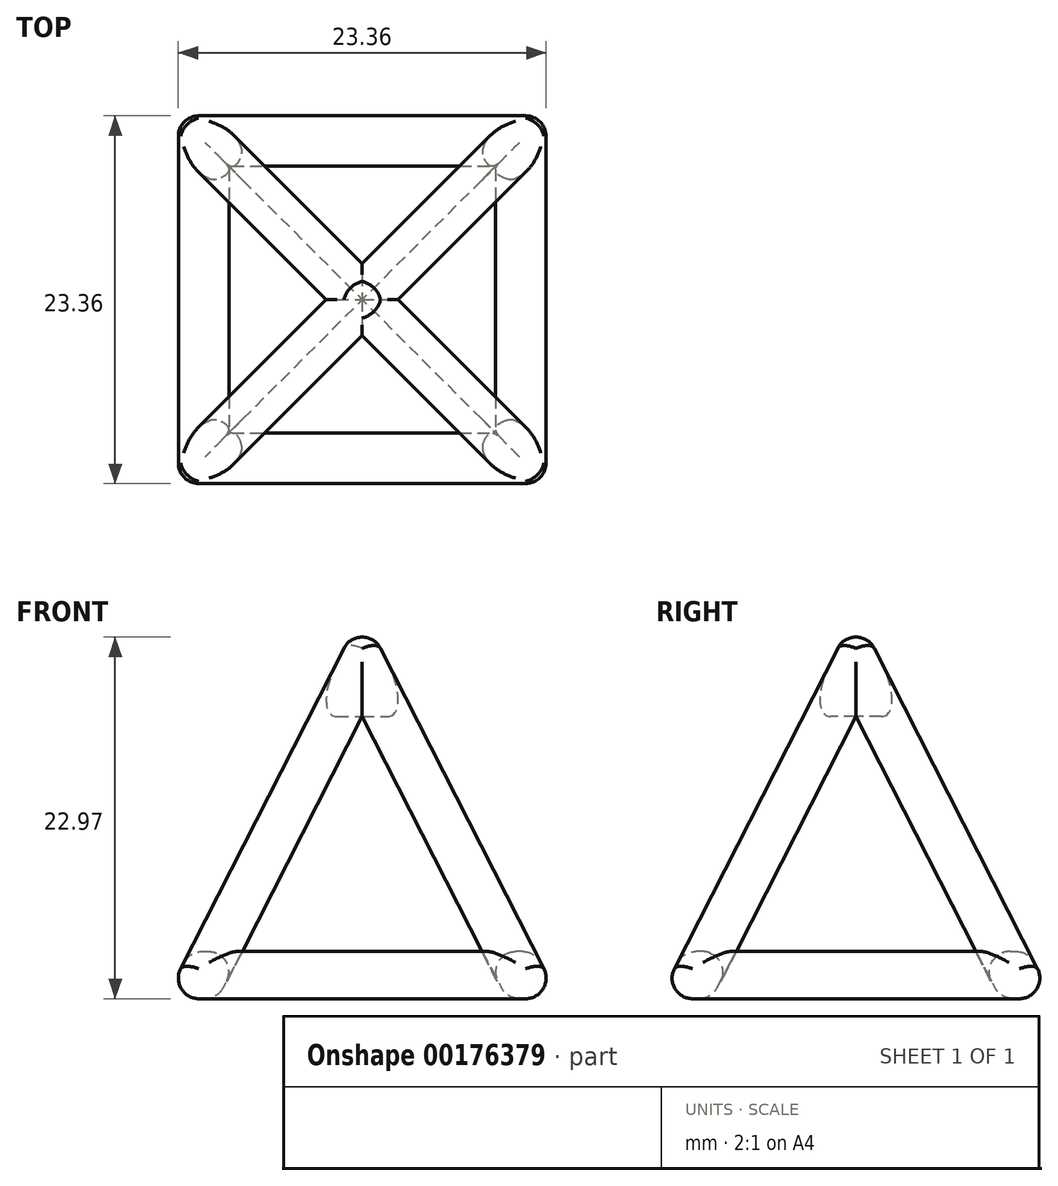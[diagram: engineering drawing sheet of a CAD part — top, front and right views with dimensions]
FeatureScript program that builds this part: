
annotation { "Feature Type Name" : "Feature", "Feature Type Description" : "" }
export const myFeature = defineFeature(function(context is Context, id is Id, definition is map)
    precondition{}
    {
        {
            var Q0;
            Q0=qCreatedBy(makeId("Top.planeOp"),FACE);
            cPlane(context, id + "F0", {"entities" : qUnion([Q0]), "cplaneType" : CPlaneType.OFFSET, "offset" : 25 * mm, "width" : 150 * mm, "height" : 150 * mm});
        }
        {
            var Q0;
            Q0=qCreatedBy(makeId("Top.planeOp"),FACE);
            var sketch = newSketch(context, id + "F1", { "sketchPlane" : qUnion([Q0])});
            skLineSegment(sketch, "E0.bottom", {"start": v(12.5, -12.5) * mm, "end": v(-12.5, -12.5) * mm});
            skLineSegment(sketch, "E0.top", {"start": v(12.5, 12.5) * mm, "end": v(-12.5, 12.5) * mm});
            skLineSegment(sketch, "E0.left", {"start": v(12.5, -12.5) * mm, "end": v(12.5, 12.5) * mm});
            skLineSegment(sketch, "E0.right", {"start": v(-12.5, -12.5) * mm, "end": v(-12.5, 12.5) * mm});
            skPoint(sketch, "E0.middle", {"position": v(0, 0) * mm});
            skSolve(sketch);
        }
        {
            var Q0;
            Q0 = qSketchRegion(id + "F1", true);
            extrude(context, id + "F2", {"entities" : qUnion([Q0]), "depth" : 30 * mm, "hasDraft" : true, "draftAngle" : 27 * degree, "draftPullDirection" : true});
        }
        {
            var Q0;
            Q0=makeQuery(id+"F2.opExtrude","CAP_FACE",FACE,{"disambiguationData":[OSD([sQuery(id+"F1.wireOp",EDGE,"E0.bottom"),sQuery(id+"F1.wireOp",EDGE,"E0.top"),sQuery(id+"F1.wireOp",EDGE,"E0.left"),sQuery(id+"F1.wireOp",EDGE,"E0.right")])],"isStart":true});
            var sketch = newSketch(context, id + "F3", { "sketchPlane" : qUnion([Q0])});
            skLineSegment(sketch, "E1.0", {"start": v(9.2, 9.2) * mm, "end": v(-9.2, 9.2) * mm});
            skLineSegment(sketch, "E1.1", {"start": v(9.2, 9.2) * mm, "end": v(9.2, -9.2) * mm});
            skLineSegment(sketch, "E1.2", {"start": v(9.2, -9.2) * mm, "end": v(-9.2, -9.2) * mm});
            skLineSegment(sketch, "E1.3", {"start": v(-9.2, 9.2) * mm, "end": v(-9.2, -9.2) * mm});
            skSolve(sketch);
        }
        {
            var Q0;
            Q0 = qSketchRegion(id + "F3", true);
            extrude(context, id + "F4", {"entities" : qUnion([Q0]), "operationType" : NewBodyOperationType.REMOVE, "oppositeDirection" : true, "depth" : 25 * mm, "hasDraft" : true, "draftAngle" : 28 * degree, "draftPullDirection" : true});
        }
        {
            var Q0;
            Q0=qCreatedBy(makeId("Front.planeOp"),FACE);
            var sketch = newSketch(context, id + "F5", { "sketchPlane" : qUnion([Q0])});
            skLineSegment(sketch, "E2.0", {"start": v(0, 17.92) * mm, "end": v(-7.6, 3) * mm});
            skLineSegment(sketch, "E2.1", {"start": v(0, 17.92) * mm, "end": v(7.6, 3) * mm});
            skLineSegment(sketch, "E2.2", {"start": v(7.6, 3) * mm, "end": v(-7.6, 3) * mm});
            skSolve(sketch);
        }
        {
            var Q0;
            Q0 = qSketchRegion(id + "F5", true);
            extrude(context, id + "F6", {"entities" : qUnion([Q0]), "operationType" : NewBodyOperationType.REMOVE, "oppositeDirection" : true, "depth" : 25 * mm, "hasSecondDirection" : true, "secondDirectionOppositeDirection" : false, "secondDirectionDepth" : 25 * mm});
        }
        {
            var Q0;
            Q0=qCreatedBy(makeId("Right.planeOp"),FACE);
            var sketch = newSketch(context, id + "F7", { "sketchPlane" : qUnion([Q0])});
            skLineSegment(sketch, "E3.0", {"start": v(0, 17.92) * mm, "end": v(7.6, 3) * mm});
            skLineSegment(sketch, "E3.1", {"start": v(0, 17.92) * mm, "end": v(-7.6, 3) * mm});
            skLineSegment(sketch, "E3.2", {"start": v(-7.6, 3) * mm, "end": v(7.6, 3) * mm});
            skSolve(sketch);
        }
        {
            var Q0;
            Q0 = qSketchRegion(id + "F7", true);
            extrude(context, id + "F8", {"entities" : qUnion([Q0]), "operationType" : NewBodyOperationType.REMOVE, "oppositeDirection" : true, "depth" : 25 * mm, "hasSecondDirection" : true, "secondDirectionOppositeDirection" : false, "secondDirectionDepth" : 25 * mm});
        }
        {
            var Q0;
            Q0=makeQuery(id+"F2.opExtrude","SWEPT_FACE",FACE,{"disambiguationData":[OSD([sQuery(id+"F1.wireOp",EDGE,"E0.bottom")])]});
            var Q1;
            Q1=makeQuery(id+"F2.opExtrude","SWEPT_FACE",FACE,{"disambiguationData":[OSD([sQuery(id+"F1.wireOp",EDGE,"E0.top")])]});
            var Q2;
            Q2=makeQuery(id+"F2.opExtrude","CAP_FACE",FACE,{"disambiguationData":[OSD([sQuery(id+"F1.wireOp",EDGE,"E0.bottom"),sQuery(id+"F1.wireOp",EDGE,"E0.top"),sQuery(id+"F1.wireOp",EDGE,"E0.left"),sQuery(id+"F1.wireOp",EDGE,"E0.right")])],"isStart":true});
            var Q3;
            Q3=makeQuery(id+"F8.boolean.opBoolean","INTERSECT",EDGE,{"derivedFrom":[makeQuery(id+"F2.opExtrude","SWEPT_FACE",FACE,{"disambiguationData":[OSD([sQuery(id+"F1.wireOp",EDGE,"E0.left")])]}),makeQuery(id+"F8.opExtrude","SWEPT_FACE",FACE,{"disambiguationData":[OSD([sQuery(id+"F7.wireOp",EDGE,"E3.2")])]})]});
            var Q4;
            Q4=makeQuery(id+"F8.boolean.opBoolean","INTERSECT",EDGE,{"derivedFrom":[makeQuery(id+"F2.opExtrude","SWEPT_FACE",FACE,{"disambiguationData":[OSD([sQuery(id+"F1.wireOp",EDGE,"E0.left")])]}),makeQuery(id+"F8.opExtrude","SWEPT_FACE",FACE,{"disambiguationData":[OSD([sQuery(id+"F7.wireOp",EDGE,"E3.0")])]})]});
            var Q5;
            Q5=makeQuery(id+"F8.boolean.opBoolean","INTERSECT",EDGE,{"derivedFrom":[makeQuery(id+"F2.opExtrude","SWEPT_FACE",FACE,{"disambiguationData":[OSD([sQuery(id+"F1.wireOp",EDGE,"E0.left")])]}),makeQuery(id+"F8.opExtrude","SWEPT_FACE",FACE,{"disambiguationData":[OSD([sQuery(id+"F7.wireOp",EDGE,"E3.1")])]})]});
            var Q6;
            Q6=makeQuery(id+"F8.boolean.opBoolean","INTERSECT",EDGE,{"derivedFrom":[makeQuery(id+"F2.opExtrude","SWEPT_FACE",FACE,{"disambiguationData":[OSD([sQuery(id+"F1.wireOp",EDGE,"E0.right")])]}),makeQuery(id+"F8.opExtrude","SWEPT_FACE",FACE,{"disambiguationData":[OSD([sQuery(id+"F7.wireOp",EDGE,"E3.1")])]})]});
            var Q7;
            Q7=makeQuery(id+"F8.boolean.opBoolean","INTERSECT",EDGE,{"derivedFrom":[makeQuery(id+"F2.opExtrude","SWEPT_FACE",FACE,{"disambiguationData":[OSD([sQuery(id+"F1.wireOp",EDGE,"E0.right")])]}),makeQuery(id+"F8.opExtrude","SWEPT_FACE",FACE,{"disambiguationData":[OSD([sQuery(id+"F7.wireOp",EDGE,"E3.0")])]})]});
            var Q8;
            Q8=makeQuery(id+"F8.boolean.opBoolean","INTERSECT",EDGE,{"derivedFrom":[makeQuery(id+"F2.opExtrude","SWEPT_FACE",FACE,{"disambiguationData":[OSD([sQuery(id+"F1.wireOp",EDGE,"E0.right")])]}),makeQuery(id+"F8.opExtrude","SWEPT_FACE",FACE,{"disambiguationData":[OSD([sQuery(id+"F7.wireOp",EDGE,"E3.2")])]})]});
            fillet(context, id + "F9", {"entities" : qUnion([Q0, Q1, Q2, Q3, Q4, Q5, Q6, Q7, Q8]), "radius" : 1.3 * mm, "tangentPropagation" : true, "allowEdgeOverflow" : false});
        }
        {
            var Q0;
            Q0=makeQuery(id+"F6.boolean.opBoolean","INTERSECT",EDGE,{"derivedFrom":[makeQuery(id+"F4.boolean.opBoolean","COPY",FACE,{"derivedFrom":makeQuery(id+"F4.opExtrude","SWEPT_FACE",FACE,{"disambiguationData":[OSD([sQuery(id+"F3.wireOp",EDGE,"E1.0")])]})}),makeQuery(id+"F6.opExtrude","SWEPT_FACE",FACE,{"disambiguationData":[OSD([sQuery(id+"F5.wireOp",EDGE,"E2.2")])]})]});
            var Q1;
            Q1=makeQuery(id+"F8.boolean.opBoolean","INTERSECT",EDGE,{"derivedFrom":[makeQuery(id+"F4.boolean.opBoolean","COPY",FACE,{"derivedFrom":makeQuery(id+"F4.opExtrude","SWEPT_FACE",FACE,{"disambiguationData":[OSD([sQuery(id+"F3.wireOp",EDGE,"E1.1")])]})}),makeQuery(id+"F8.opExtrude","SWEPT_FACE",FACE,{"disambiguationData":[OSD([sQuery(id+"F7.wireOp",EDGE,"E3.2")])]})]});
            var Q2;
            Q2=makeQuery(id+"F6.boolean.opBoolean","INTERSECT",EDGE,{"derivedFrom":[makeQuery(id+"F4.boolean.opBoolean","COPY",FACE,{"derivedFrom":makeQuery(id+"F4.opExtrude","SWEPT_FACE",FACE,{"disambiguationData":[OSD([sQuery(id+"F3.wireOp",EDGE,"E1.2")])]})}),makeQuery(id+"F6.opExtrude","SWEPT_FACE",FACE,{"disambiguationData":[OSD([sQuery(id+"F5.wireOp",EDGE,"E2.2")])]})]});
            var Q3;
            Q3=makeQuery(id+"F8.boolean.opBoolean","INTERSECT",EDGE,{"derivedFrom":[makeQuery(id+"F4.boolean.opBoolean","COPY",FACE,{"derivedFrom":makeQuery(id+"F4.opExtrude","SWEPT_FACE",FACE,{"disambiguationData":[OSD([sQuery(id+"F3.wireOp",EDGE,"E1.3")])]})}),makeQuery(id+"F8.opExtrude","SWEPT_FACE",FACE,{"disambiguationData":[OSD([sQuery(id+"F7.wireOp",EDGE,"E3.2")])]})]});
            fillet(context, id + "F10", {"entities" : qUnion([Q0, Q1, Q2, Q3]), "radius" : 1.3 * mm, "tangentPropagation" : true, "allowEdgeOverflow" : false});
        }
    });
